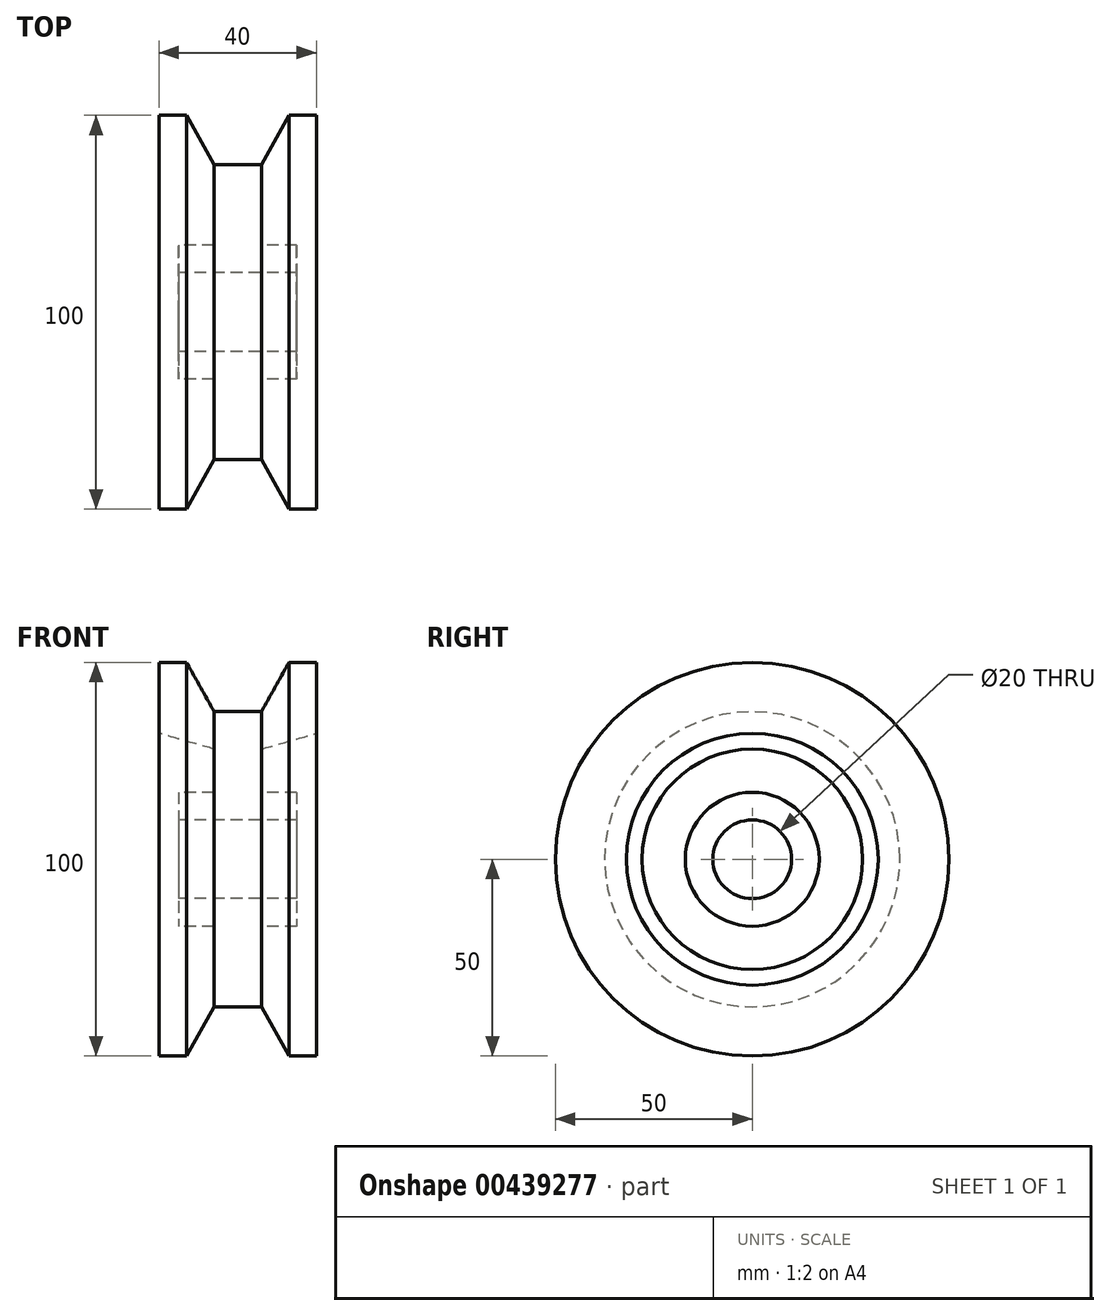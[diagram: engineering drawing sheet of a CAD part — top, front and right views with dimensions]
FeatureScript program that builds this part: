
annotation { "Feature Type Name" : "Feature", "Feature Type Description" : "" }
export const myFeature = defineFeature(function(context is Context, id is Id, definition is map)
    precondition{}
    {
        {
            var Q0;
            Q0=qCreatedBy(makeId("Front.planeOp"),FACE);
            var sketch = newSketch(context, id + "F0", { "sketchPlane" : qUnion([Q0])});
            skLineSegment(sketch, "E0", {"start": v(0, 0) * mm, "end": v(15.74, 0) * mm});
            skLineSegment(sketch, "E1", {"start": v(-15, -17) * mm, "end": v(-15, -10) * mm});
            skLineSegment(sketch, "E2", {"start": v(-15, -10) * mm, "end": v(15, -10) * mm});
            skLineSegment(sketch, "E3", {"start": v(15, -10) * mm, "end": v(15, -17) * mm});
            skLineSegment(sketch, "E4", {"start": v(15, -17) * mm, "end": v(6, -17) * mm});
            skLineSegment(sketch, "E5", {"start": v(6, -17) * mm, "end": v(6, -28) * mm});
            skLineSegment(sketch, "E6", {"start": v(-15, -17) * mm, "end": v(-6, -17) * mm});
            skLineSegment(sketch, "E7", {"start": v(-6, -17) * mm, "end": v(-6, -28) * mm});
            skLineSegment(sketch, "E8", {"start": v(-6, -28) * mm, "end": v(-20, -32) * mm});
            skLineSegment(sketch, "E9", {"start": v(6, -28) * mm, "end": v(20, -32) * mm});
            skLineSegment(sketch, "E10", {"start": v(-20, -32) * mm, "end": v(-20, -50) * mm});
            skLineSegment(sketch, "E11", {"start": v(-20, -50) * mm, "end": v(-13, -50) * mm});
            skLineSegment(sketch, "E12", {"start": v(-13, -50) * mm, "end": v(-6, -37.5) * mm});
            skLineSegment(sketch, "E13", {"start": v(-6, -37.5) * mm, "end": v(6, -37.5) * mm});
            skLineSegment(sketch, "E14", {"start": v(6, -37.5) * mm, "end": v(13, -50) * mm});
            skLineSegment(sketch, "E15", {"start": v(13, -50) * mm, "end": v(20, -50) * mm});
            skLineSegment(sketch, "E16", {"start": v(20, -50) * mm, "end": v(20, -32) * mm});
            skSolve(sketch);
        }
        {
            var Q0;
            Q0=makeQuery(id+"F0.imprint","IMPRINT",FACE,{"disambiguationData":[TD([[makeQuery(id+"F0.imprint","IMPRINT",EDGE,{"derivedFrom":sQuery(id+"F0.wireOp",EDGE,"E1")}),-1.0]])]});
            var Q1;
            Q1=sQuery(id+"F0.wireOp",EDGE,"E0");
            revolve(context, id + "F1", {"entities" : qUnion([Q0]), "axis" : qUnion([Q1]), "revolveType" : RevolveType.FULL});
        }
    });
